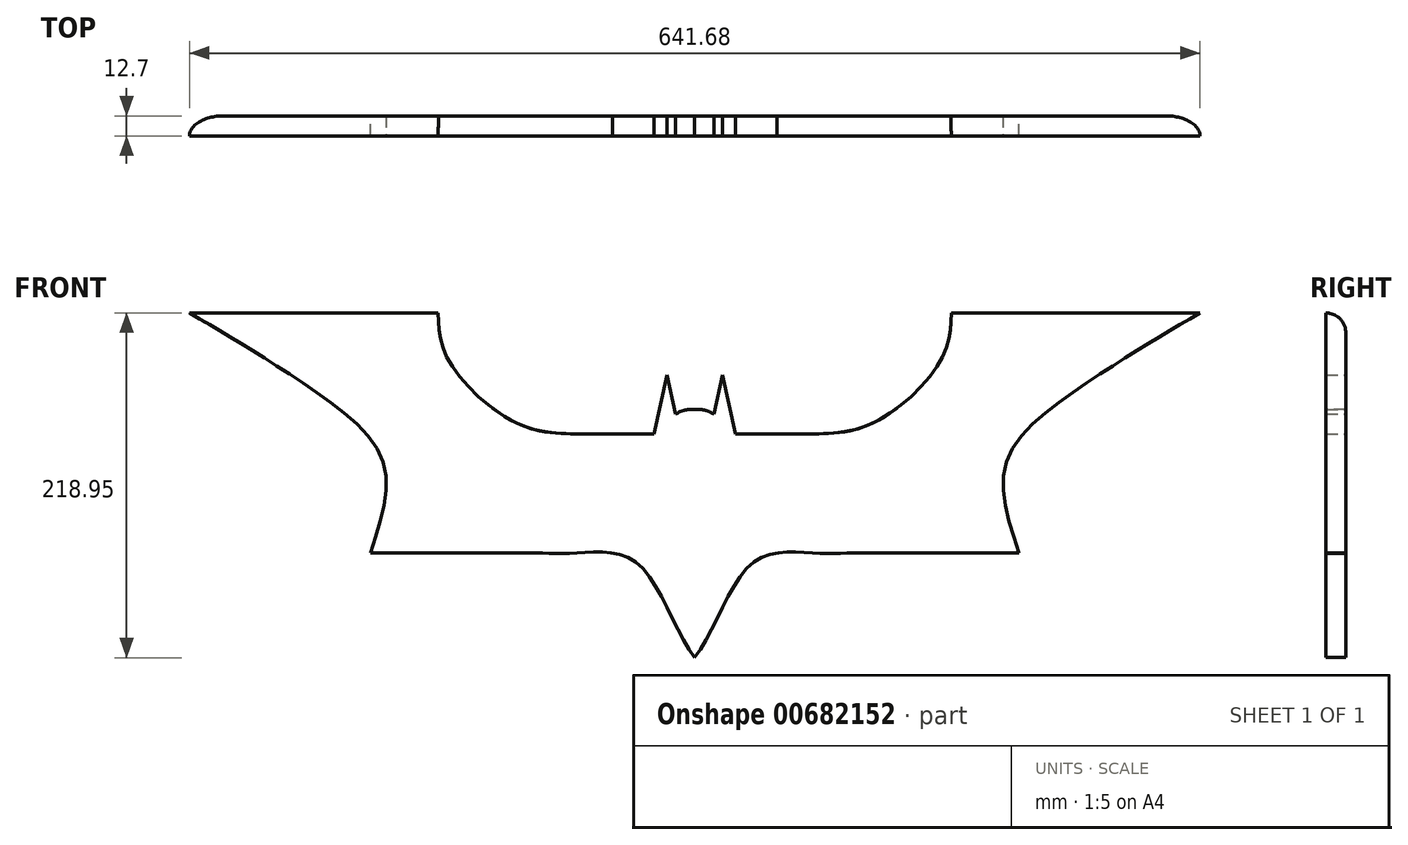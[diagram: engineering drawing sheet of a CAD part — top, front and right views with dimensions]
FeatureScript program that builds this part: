
annotation { "Feature Type Name" : "Feature", "Feature Type Description" : "" }
export const myFeature = defineFeature(function(context is Context, id is Id, definition is map)
    precondition{}
    {
        {
            var Q0;
            Q0=qCreatedBy(makeId("Front.planeOp"),FACE);
            var sketch = newSketch(context, id + "F0", { "sketchPlane" : qUnion([Q0])});
            skFitSpline(sketch, "E0", {"points": [v(0, 22.16) * mm, v(-12.1, 19.07) * mm], "startDerivative": vector(-13.82, 0.85) * mm, "endDerivative": vector(-9.82, -7.06) * mm});
            skLineSegment(sketch, "E1", {"start": v(-12.1, 19.07) * mm, "end": v(-17.71, 43.9) * mm});
            skLineSegment(sketch, "E2", {"start": v(-17.71, 43.9) * mm, "end": v(-25.86, 6.6) * mm});
            skLineSegment(sketch, "E3", {"start": v(-25.86, 6.6) * mm, "end": v(-52.17, 6.6) * mm});
            skLineSegment(sketch, "E4", {"start": v(-152.2, -69.18) * mm, "end": v(-100.34, -69.18) * mm});
            skFitSpline(sketch, "E5", {"points": [v(-100.34, -69.18) * mm, v(-75.64, -69.18) * mm, v(-36.62, -75.6) * mm, v(0, -135.58) * mm], "startDerivative": vector(84.8, 0.5) * mm, "endDerivative": vector(87.47, -108) * mm});
            skLineSegment(sketch, "E6.MirrorCS", {"start": v(152.2, -69.18) * mm, "end": v(100.34, -69.18) * mm});
            skLineSegment(sketch, "E7.MirrorCS", {"start": v(25.86, 6.6) * mm, "end": v(52.17, 6.6) * mm});
            skLineSegment(sketch, "E8.MirrorCS", {"start": v(17.71, 43.9) * mm, "end": v(25.86, 6.6) * mm});
            skLineSegment(sketch, "E9.MirrorCS", {"start": v(12.1, 19.07) * mm, "end": v(17.71, 43.9) * mm});
            skFitSpline(sketch, "E10.MirrorCS", {"points": [v(0, 22.16) * mm, v(12.1, 19.07) * mm], "startDerivative": vector(13.82, 0.85) * mm, "endDerivative": vector(9.82, -7.06) * mm});
            skFitSpline(sketch, "E11.MirrorCS", {"points": [v(100.34, -69.18) * mm, v(75.64, -69.18) * mm, v(36.62, -75.6) * mm, v(0, -135.58) * mm], "startDerivative": vector(-84.8, 0.5) * mm, "endDerivative": vector(-87.47, -108) * mm});
            skFitSpline(sketch, "E12", {"points": [v(-52.17, 6.6) * mm, v(-77.74, 6.6) * mm, v(-114.3, 13.95) * mm, v(-157.07, 54.65) * mm, v(-162.89, 83.37) * mm], "startDerivative": vector(-118.47, -1.26) * mm, "endDerivative": vector(-2.53, 122.43) * mm});
            skLineSegment(sketch, "E13", {"start": v(-162.89, 83.37) * mm, "end": v(-320.84, 83.37) * mm});
            skFitSpline(sketch, "E14", {"points": [v(-320.84, 83.37) * mm, v(-289.95, 65.07) * mm, v(-243.89, 35.43) * mm, v(-198.18, -10.74) * mm, v(-206.04, -69.07) * mm], "startDerivative": vector(144.2, -85.05) * mm, "endDerivative": vector(-77.68, -233.24) * mm});
            skLineSegment(sketch, "E15", {"start": v(-206.04, -69.07) * mm, "end": v(-152.2, -69.18) * mm});
            skFitSpline(sketch, "E16.MirrorCS", {"points": [v(320.84, 83.37) * mm, v(289.95, 65.07) * mm, v(243.89, 35.43) * mm, v(198.18, -10.74) * mm, v(206.04, -69.07) * mm], "startDerivative": vector(-144.2, -85.05) * mm, "endDerivative": vector(77.68, -233.24) * mm});
            skLineSegment(sketch, "E17.MirrorCS", {"start": v(162.89, 83.37) * mm, "end": v(320.84, 83.37) * mm});
            skFitSpline(sketch, "E18.MirrorCS", {"points": [v(52.17, 6.6) * mm, v(77.74, 6.6) * mm, v(114.3, 13.95) * mm, v(157.07, 54.65) * mm, v(162.89, 83.37) * mm], "startDerivative": vector(118.47, -1.26) * mm, "endDerivative": vector(2.53, 122.43) * mm});
            skLineSegment(sketch, "E19.MirrorCS", {"start": v(206.04, -69.07) * mm, "end": v(152.2, -69.18) * mm});
            skSolve(sketch);
        }
        {
            var Q0;
            Q0=makeQuery(id+"F0.imprint","IMPRINT",FACE,{"disambiguationData":[TD([[makeQuery(id+"F0.imprint","IMPRINT",EDGE,{"derivedFrom":sQuery(id+"F0.wireOp",EDGE,"E0")}),1.0]])]});
            extrude(context, id + "F1", {"entities" : qUnion([Q0]), "depth" : 12.7 * mm, "offsetDistance" : 25.4 * mm});
        }
        {
            var Q0;
            Q0=makeQuery(id+"F1.opExtrude","CAP_EDGE",EDGE,{"disambiguationData":[OSD([sQuery(id+"F0.wireOp",EDGE,"E17.MirrorCS")])],"isStart":true});
            fillet(context, id + "F2", {"entities" : qUnion([Q0]), "radius" : 12.7 * mm, "tangentPropagation" : true, "allowEdgeOverflow" : false});
        }
        {
            var Q0;
            Q0=makeQuery(id+"F1.opExtrude","CAP_EDGE",EDGE,{"disambiguationData":[OSD([sQuery(id+"F0.wireOp",EDGE,"E13")])],"isStart":true});
            fillet(context, id + "F3", {"entities" : qUnion([Q0]), "radius" : 12.7 * mm, "tangentPropagation" : true, "allowEdgeOverflow" : false});
        }
    });
